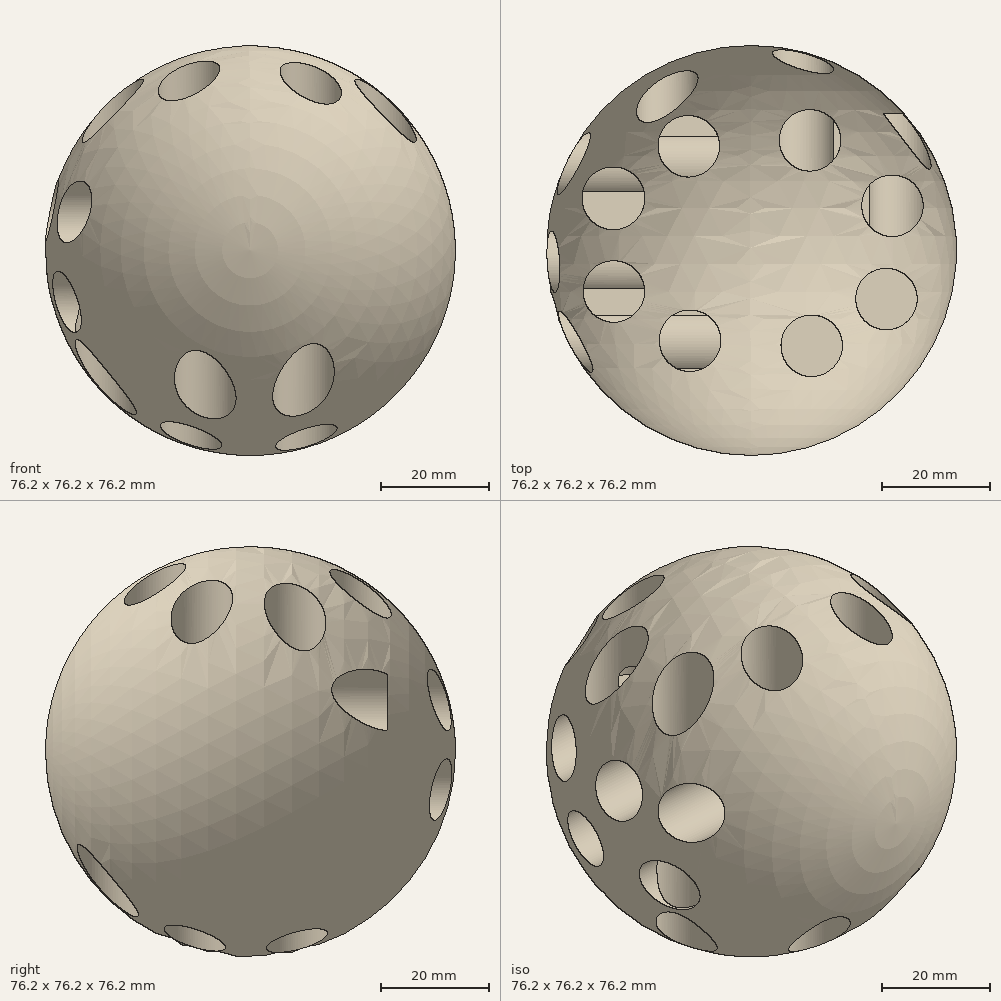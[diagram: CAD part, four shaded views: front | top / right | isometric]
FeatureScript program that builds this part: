
annotation { "Feature Type Name" : "Feature", "Feature Type Description" : "" }
export const myFeature = defineFeature(function(context is Context, id is Id, definition is map)
    precondition{}
    {
        {
            var Q0;
            Q0=qCreatedBy(makeId("Top.planeOp"),FACE);
            var sketch = newSketch(context, id + "F0", { "sketchPlane" : qUnion([Q0])});
            skArc(sketch, "E0", {"start": v(0, -38.1) * mm, "mid": v(38.1, 0) * mm, "end": v(0, 38.1) * mm});
            skLineSegment(sketch, "E1", {"start": v(0, 38.1) * mm, "end": v(0, -38.1) * mm});
            skSolve(sketch);
        }
        {
            var Q0;
            Q0=makeQuery(id+"F0.imprint","IMPRINT",FACE,{"disambiguationData":[TD([[makeQuery(id+"F0.imprint","IMPRINT",EDGE,{"derivedFrom":sQuery(id+"F0.wireOp",EDGE,"E0")}),1.0]])]});
            var Q1;
            Q1=sQuery(id+"F0.wireOp",EDGE,"E1");
            revolve(context, id + "F1", {"entities" : qUnion([Q0]), "axis" : qUnion([Q1]), "revolveType" : RevolveType.FULL});
        }
        {
            var Q0;
            Q0=qCreatedBy(makeId("Top.planeOp"),FACE);
            cPlane(context, id + "F2", {"entities" : qUnion([Q0]), "cplaneType" : CPlaneType.OFFSET, "offset" : 35.56 * mm, "width" : 152.4 * mm, "height" : 152.4 * mm});
        }
        {
            var Q0;
            Q0=qCreatedBy(id+"F2.planeOp",FACE);
            var sketch = newSketch(context, id + "F3", { "sketchPlane" : qUnion([Q0])});
            skCircle(sketch, "E2", {"center": v(-25.68, 9.68) * mm, "radius": 5.84 * mm});
            skSolve(sketch);
        }
        {
            var Q0;
            Q0 = qSketchRegion(id + "F3", true);
            extrude(context, id + "F4", {"entities" : qUnion([Q0]), "operationType" : NewBodyOperationType.REMOVE, "oppositeDirection" : true, "depth" : 25.4 * mm});
        }
        {
            var Q0;
            Q0=qCreatedBy(id+"F2.planeOp",FACE);
            var sketch = newSketch(context, id + "F5", { "sketchPlane" : qUnion([Q0])});
            skCircle(sketch, "E3", {"center": v(-25.59, -7.63) * mm, "radius": 5.71 * mm});
            skSolve(sketch);
        }
        {
            var Q0;
            Q0=makeQuery(id+"F5.imprint","IMPRINT",FACE,{"disambiguationData":[TD([[makeQuery(id+"F5.imprint","IMPRINT",EDGE,{"derivedFrom":sQuery(id+"F5.wireOp",EDGE,"E3")}),1.0]])]});
            extrude(context, id + "F6", {"entities" : qUnion([Q0]), "operationType" : NewBodyOperationType.REMOVE, "oppositeDirection" : true, "depth" : 25.4 * mm});
        }
        {
            var Q0;
            Q0=qCreatedBy(id+"F2.planeOp",FACE);
            var sketch = newSketch(context, id + "F7", { "sketchPlane" : qUnion([Q0])});
            skCircle(sketch, "E4", {"center": v(-11.67, 19.36) * mm, "radius": 5.72 * mm});
            skSolve(sketch);
        }
        {
            var Q0;
            Q0 = qSketchRegion(id + "F7", true);
            extrude(context, id + "F8", {"entities" : qUnion([Q0]), "operationType" : NewBodyOperationType.REMOVE, "oppositeDirection" : true, "depth" : 25.4 * mm});
        }
        {
            var Q0;
            Q0=qCreatedBy(id+"F2.planeOp",FACE);
            var sketch = newSketch(context, id + "F9", { "sketchPlane" : qUnion([Q0])});
            skCircle(sketch, "E5", {"center": v(-11.43, -16.78) * mm, "radius": 5.72 * mm});
            skSolve(sketch);
        }
        {
            var Q0;
            Q0 = qSketchRegion(id + "F9", true);
            extrude(context, id + "F10", {"entities" : qUnion([Q0]), "operationType" : NewBodyOperationType.REMOVE, "oppositeDirection" : true, "depth" : 25.4 * mm});
        }
        {
            var Q0;
            Q0=qCreatedBy(id+"F2.planeOp",FACE);
            var sketch = newSketch(context, id + "F11", { "sketchPlane" : qUnion([Q0])});
            skCircle(sketch, "E6", {"center": v(10.88, 20.46) * mm, "radius": 5.72 * mm});
            skSolve(sketch);
        }
        {
            var Q0;
            Q0 = qSketchRegion(id + "F11", true);
            extrude(context, id + "F12", {"entities" : qUnion([Q0]), "operationType" : NewBodyOperationType.REMOVE, "oppositeDirection" : true, "depth" : 25.4 * mm});
        }
        {
            var Q0;
            Q0=qCreatedBy(id+"F2.planeOp",FACE);
            var sketch = newSketch(context, id + "F13", { "sketchPlane" : qUnion([Q0])});
            skCircle(sketch, "E7", {"center": v(26.18, 8.3) * mm, "radius": 5.72 * mm});
            skSolve(sketch);
        }
        {
            var Q0;
            Q0 = qSketchRegion(id + "F13", true);
            extrude(context, id + "F14", {"entities" : qUnion([Q0]), "operationType" : NewBodyOperationType.REMOVE, "oppositeDirection" : true, "depth" : 25.4 * mm});
        }
        {
            var Q0;
            Q0=qCreatedBy(id+"F2.planeOp",FACE);
            var sketch = newSketch(context, id + "F15", { "sketchPlane" : qUnion([Q0])});
            skCircle(sketch, "E8", {"center": v(11.17, -17.72) * mm, "radius": 5.72 * mm});
            skSolve(sketch);
        }
        {
            var Q0;
            Q0 = qSketchRegion(id + "F15", true);
            extrude(context, id + "F16", {"entities" : qUnion([Q0]), "operationType" : NewBodyOperationType.REMOVE, "oppositeDirection" : true, "depth" : 25.4 * mm});
        }
        {
            var Q0;
            Q0=qCreatedBy(id+"F2.planeOp",FACE);
            var sketch = newSketch(context, id + "F17", { "sketchPlane" : qUnion([Q0])});
            skCircle(sketch, "E9", {"center": v(25.07, -9.03) * mm, "radius": 5.71 * mm});
            skSolve(sketch);
        }
        {
            var Q0;
            Q0 = qSketchRegion(id + "F17", true);
            extrude(context, id + "F18", {"entities" : qUnion([Q0]), "operationType" : NewBodyOperationType.REMOVE, "oppositeDirection" : true, "depth" : 25.4 * mm});
        }
        {
            var Q0;
            Q0=qCreatedBy(makeId("Top.planeOp"),FACE);
            var sketch = newSketch(context, id + "F19", { "sketchPlane" : qUnion([Q0])});
            skCircle(sketch, "E10", {"center": v(-11.02, -10.7) * mm, "radius": 5.72 * mm});
            skSolve(sketch);
        }
        {
            var Q0;
            Q0 = qSketchRegion(id + "F19", true);
            extrude(context, id + "F20", {"entities" : qUnion([Q0]), "operationType" : NewBodyOperationType.REMOVE, "oppositeDirection" : true, "depth" : 50.8 * mm});
        }
        {
            var Q0;
            Q0=qCreatedBy(makeId("Top.planeOp"),FACE);
            var sketch = newSketch(context, id + "F21", { "sketchPlane" : qUnion([Q0])});
            skCircle(sketch, "E11", {"center": v(-8.41, -26.27) * mm, "radius": 5.72 * mm});
            skSolve(sketch);
        }
        {
            var Q0;
            Q0 = qSketchRegion(id + "F21", true);
            extrude(context, id + "F22", {"entities" : qUnion([Q0]), "operationType" : NewBodyOperationType.REMOVE, "oppositeDirection" : true, "depth" : 38.1 * mm});
        }
        {
            var Q0;
            Q0=qCreatedBy(makeId("Top.planeOp"),FACE);
            var sketch = newSketch(context, id + "F23", { "sketchPlane" : qUnion([Q0])});
            skCircle(sketch, "E12", {"center": v(-26.86, -9.87) * mm, "radius": 5.71 * mm});
            skSolve(sketch);
        }
        {
            var Q0;
            Q0 = qSketchRegion(id + "F23", true);
            extrude(context, id + "F24", {"entities" : qUnion([Q0]), "operationType" : NewBodyOperationType.REMOVE, "oppositeDirection" : true, "depth" : 50.8 * mm});
        }
        {
            var Q0;
            Q0=qCreatedBy(makeId("Top.planeOp"),FACE);
            var sketch = newSketch(context, id + "F25", { "sketchPlane" : qUnion([Q0])});
            skCircle(sketch, "E13", {"center": v(10.36, -10.32) * mm, "radius": 5.72 * mm});
            skSolve(sketch);
        }
        {
            var Q0;
            Q0 = qSketchRegion(id + "F25", true);
            extrude(context, id + "F26", {"entities" : qUnion([Q0]), "operationType" : NewBodyOperationType.REMOVE, "oppositeDirection" : true, "depth" : 50.8 * mm});
        }
        {
            var Q0;
            Q0=qCreatedBy(makeId("Top.planeOp"),FACE);
            var sketch = newSketch(context, id + "F27", { "sketchPlane" : qUnion([Q0])});
            skCircle(sketch, "E14", {"center": v(9.81, -26.5) * mm, "radius": 5.72 * mm});
            skSolve(sketch);
        }
        {
            var Q0;
            Q0 = qSketchRegion(id + "F27", true);
            extrude(context, id + "F28", {"entities" : qUnion([Q0]), "operationType" : NewBodyOperationType.REMOVE, "oppositeDirection" : true, "depth" : 38.1 * mm});
        }
        {
            var Q0;
            Q0=qCreatedBy(makeId("Front.planeOp"),FACE);
            var sketch = newSketch(context, id + "F29", { "sketchPlane" : qUnion([Q0])});
            skCircle(sketch, "E15", {"center": v(9.59, 9.57) * mm, "radius": 5.72 * mm});
            skSolve(sketch);
        }
        {
            var Q0;
            Q0 = qSketchRegion(id + "F29", true);
            extrude(context, id + "F30", {"entities" : qUnion([Q0]), "operationType" : NewBodyOperationType.REMOVE, "oppositeDirection" : true, "depth" : 50.8 * mm});
        }
        {
            var Q0;
            Q0=qCreatedBy(makeId("Front.planeOp"),FACE);
            var sketch = newSketch(context, id + "F31", { "sketchPlane" : qUnion([Q0])});
            skCircle(sketch, "E16", {"center": v(-21.75, -11.15) * mm, "radius": 5.72 * mm});
            skSolve(sketch);
        }
        {
            var Q0;
            Q0 = qSketchRegion(id + "F31", true);
            extrude(context, id + "F32", {"entities" : qUnion([Q0]), "operationType" : NewBodyOperationType.REMOVE, "oppositeDirection" : true, "depth" : 50.8 * mm});
        }
        {
            var Q0;
            Q0=qCreatedBy(makeId("Top.planeOp"),FACE);
            var sketch = newSketch(context, id + "F33", { "sketchPlane" : qUnion([Q0])});
            skCircle(sketch, "E17", {"center": v(10.32, 8.66) * mm, "radius": 5.72 * mm});
            skSolve(sketch);
        }
        {
            var Q0;
            Q0 = qSketchRegion(id + "F33", true);
            extrude(context, id + "F34", {"entities" : qUnion([Q0]), "operationType" : NewBodyOperationType.REMOVE, "oppositeDirection" : true, "depth" : 50.8 * mm});
        }
        {
            var Q0;
            Q0=qCreatedBy(makeId("Top.planeOp"),FACE);
            var sketch = newSketch(context, id + "F35", { "sketchPlane" : qUnion([Q0])});
            skCircle(sketch, "E18", {"center": v(-10.88, 9.77) * mm, "radius": 5.72 * mm});
            skSolve(sketch);
        }
        {
            var Q0;
            Q0 = qSketchRegion(id + "F35", true);
            extrude(context, id + "F36", {"entities" : qUnion([Q0]), "operationType" : NewBodyOperationType.REMOVE, "oppositeDirection" : true, "depth" : 50.8 * mm});
        }
        {
            var Q0;
            Q0=qCreatedBy(makeId("Front.planeOp"),FACE);
            var sketch = newSketch(context, id + "F37", { "sketchPlane" : qUnion([Q0])});
            skCircle(sketch, "E19", {"center": v(27.64, 9.6) * mm, "radius": 5.72 * mm});
            skSolve(sketch);
        }
        {
            var Q0;
            Q0 = qSketchRegion(id + "F37", true);
            extrude(context, id + "F38", {"entities" : qUnion([Q0]), "operationType" : NewBodyOperationType.REMOVE, "oppositeDirection" : true, "depth" : 25.4 * mm});
        }
        {
            var Q0;
            Q0=qCreatedBy(makeId("Right.planeOp"),FACE);
            var sketch = newSketch(context, id + "F39", { "sketchPlane" : qUnion([Q0])});
            skCircle(sketch, "E20", {"center": v(7.21, -6.77) * mm, "radius": 5.72 * mm});
            skSolve(sketch);
        }
        {
            var Q0;
            Q0 = qSketchRegion(id + "F39", true);
            extrude(context, id + "F40", {"entities" : qUnion([Q0]), "operationType" : NewBodyOperationType.REMOVE, "oppositeDirection" : true, "depth" : 50.8 * mm});
        }
        {
            var Q0;
            Q0=qCreatedBy(makeId("Right.planeOp"),FACE);
            var sketch = newSketch(context, id + "F41", { "sketchPlane" : qUnion([Q0])});
            skCircle(sketch, "E21", {"center": v(-12.62, -9.54) * mm, "radius": 5.72 * mm});
            skSolve(sketch);
        }
        {
            var Q0;
            Q0 = qSketchRegion(id + "F41", true);
            extrude(context, id + "F42", {"entities" : qUnion([Q0]), "operationType" : NewBodyOperationType.REMOVE, "oppositeDirection" : true, "depth" : 50.8 * mm});
        }
        {
            var Q0;
            Q0=qCreatedBy(makeId("Front.planeOp"),FACE);
            var sketch = newSketch(context, id + "F43", { "sketchPlane" : qUnion([Q0])});
            skCircle(sketch, "E22", {"center": v(-15.67, 18.25) * mm, "radius": 5.72 * mm});
            skSolve(sketch);
        }
        {
            var Q0;
            Q0 = qSketchRegion(id + "F43", true);
            extrude(context, id + "F44", {"entities" : qUnion([Q0]), "operationType" : NewBodyOperationType.REMOVE, "oppositeDirection" : true, "depth" : 50.8 * mm});
        }
        {
            var Q0;
            Q0=qCreatedBy(makeId("Right.planeOp"),FACE);
            var sketch = newSketch(context, id + "F45", { "sketchPlane" : qUnion([Q0])});
            skCircle(sketch, "E23", {"center": v(-16.96, 7.19) * mm, "radius": 5.72 * mm});
            skSolve(sketch);
        }
        {
            var Q0;
            Q0 = qSketchRegion(id + "F45", true);
            extrude(context, id + "F46", {"entities" : qUnion([Q0]), "operationType" : NewBodyOperationType.REMOVE, "oppositeDirection" : true, "depth" : 50.8 * mm});
        }
        {
            var Q0;
            Q0=qCreatedBy(makeId("Right.planeOp"),FACE);
            var sketch = newSketch(context, id + "F47", { "sketchPlane" : qUnion([Q0])});
            skCircle(sketch, "E24", {"center": v(12.35, -22.3) * mm, "radius": 5.72 * mm});
            skSolve(sketch);
        }
        {
            var Q0;
            Q0 = qSketchRegion(id + "F47", true);
            extrude(context, id + "F48", {"entities" : qUnion([Q0]), "operationType" : NewBodyOperationType.REMOVE, "oppositeDirection" : true, "depth" : 25.4 * mm});
        }
        {
            var Q0;
            Q0=qCreatedBy(makeId("Front.planeOp"),FACE);
            var sketch = newSketch(context, id + "F49", { "sketchPlane" : qUnion([Q0])});
            skCircle(sketch, "E25", {"center": v(10.8, -7.06) * mm, "radius": 5.72 * mm});
            skSolve(sketch);
        }
        {
            var Q0;
            Q0 = qSketchRegion(id + "F49", true);
            extrude(context, id + "F50", {"entities" : qUnion([Q0]), "operationType" : NewBodyOperationType.REMOVE, "oppositeDirection" : true, "depth" : 50.8 * mm});
        }
        {
            var Q0;
            Q0=qCreatedBy(makeId("Right.planeOp"),FACE);
            var sketch = newSketch(context, id + "F51", { "sketchPlane" : qUnion([Q0])});
            skCircle(sketch, "E26", {"center": v(16.13, 7.65) * mm, "radius": 5.72 * mm});
            skSolve(sketch);
        }
        {
            var Q0;
            Q0 = qSketchRegion(id + "F51", true);
            extrude(context, id + "F52", {"entities" : qUnion([Q0]), "operationType" : NewBodyOperationType.REMOVE, "oppositeDirection" : true, "depth" : 50.8 * mm});
        }
        {
            var Q0;
            Q0=qCreatedBy(makeId("Right.planeOp"),FACE);
            var sketch = newSketch(context, id + "F53", { "sketchPlane" : qUnion([Q0])});
            skCircle(sketch, "E27", {"center": v(-2.1, 7.49) * mm, "radius": 5.72 * mm});
            skSolve(sketch);
        }
        {
            var Q0;
            Q0 = qSketchRegion(id + "F53", true);
            extrude(context, id + "F54", {"entities" : qUnion([Q0]), "operationType" : NewBodyOperationType.REMOVE, "oppositeDirection" : true, "depth" : 50.8 * mm});
        }
    });
